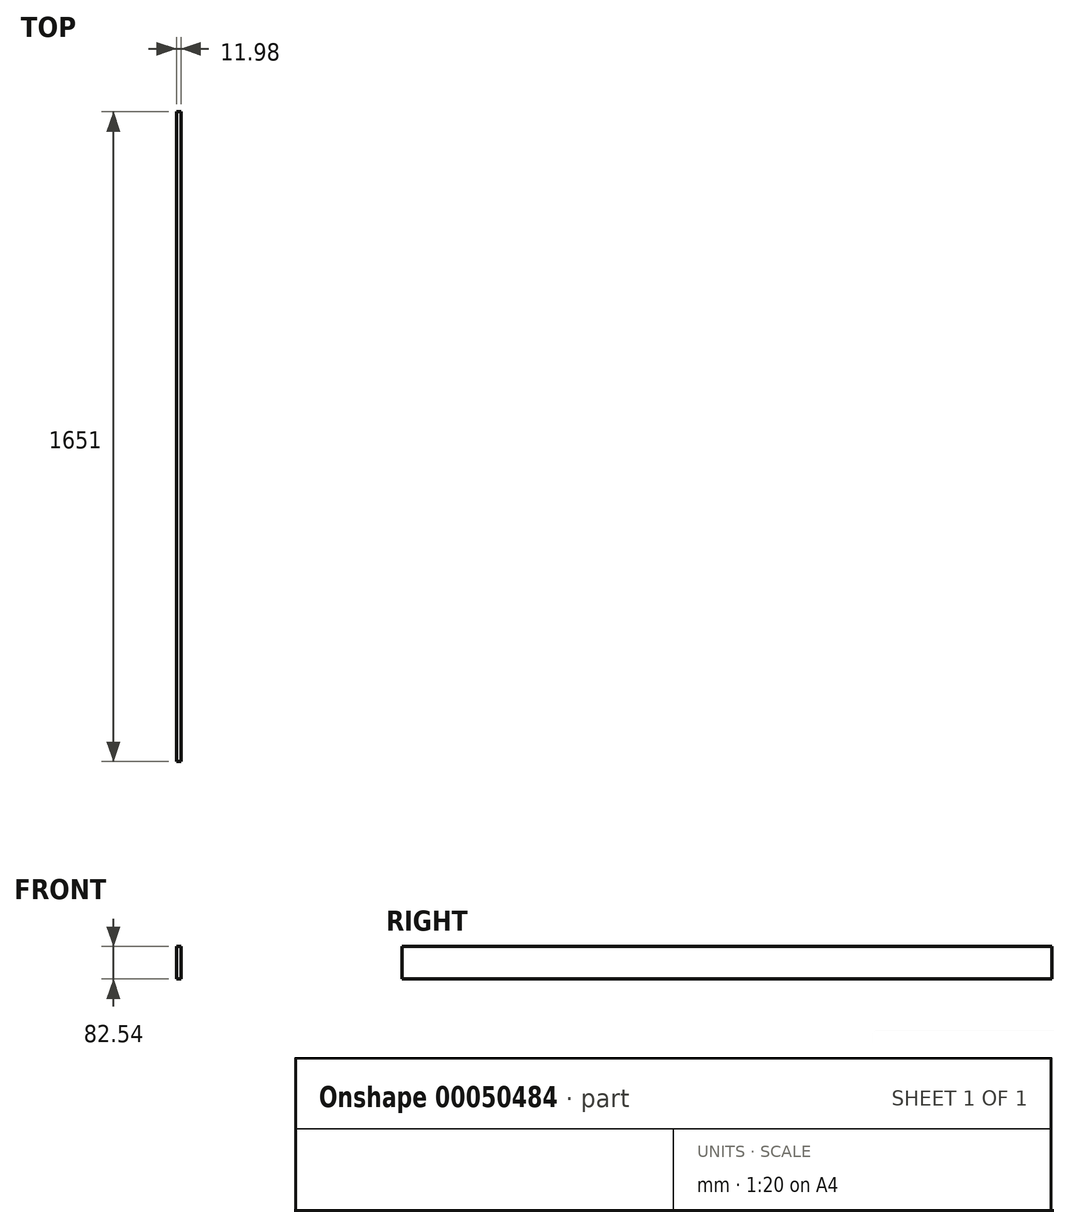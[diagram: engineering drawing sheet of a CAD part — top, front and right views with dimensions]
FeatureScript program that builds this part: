
annotation { "Feature Type Name" : "Feature", "Feature Type Description" : "" }
export const myFeature = defineFeature(function(context is Context, id is Id, definition is map)
    precondition{}
    {
        {
            var Q0;
            Q0=qCreatedBy(makeId("Right.planeOp"),FACE);
            var sketch = newSketch(context, id + "F0", { "sketchPlane" : qUnion([Q0])});
            skLineSegment(sketch, "E0.rect.bottom", {"start": v(825.5, -41.27) * mm, "end": v(-825.5, -41.28) * mm});
            skLineSegment(sketch, "E0.rect.top", {"start": v(825.5, 41.28) * mm, "end": v(-825.5, 41.27) * mm});
            skLineSegment(sketch, "E0.rect.left", {"start": v(825.5, -41.27) * mm, "end": v(825.5, 41.28) * mm});
            skLineSegment(sketch, "E0.rect.right", {"start": v(-825.5, -41.28) * mm, "end": v(-825.5, 41.27) * mm});
            skPoint(sketch, "E0.rect.middle", {"position": v(0, 0) * mm});
            skSolve(sketch);
        }
        {
            var Q0;
            Q0 = qSketchRegion(id + "F0", true);
            extrude(context, id + "F1", {"entities" : qUnion([Q0]), "endBound" : BoundingType.SYMMETRIC, "depth" : 12 * mm});
        }
    });
